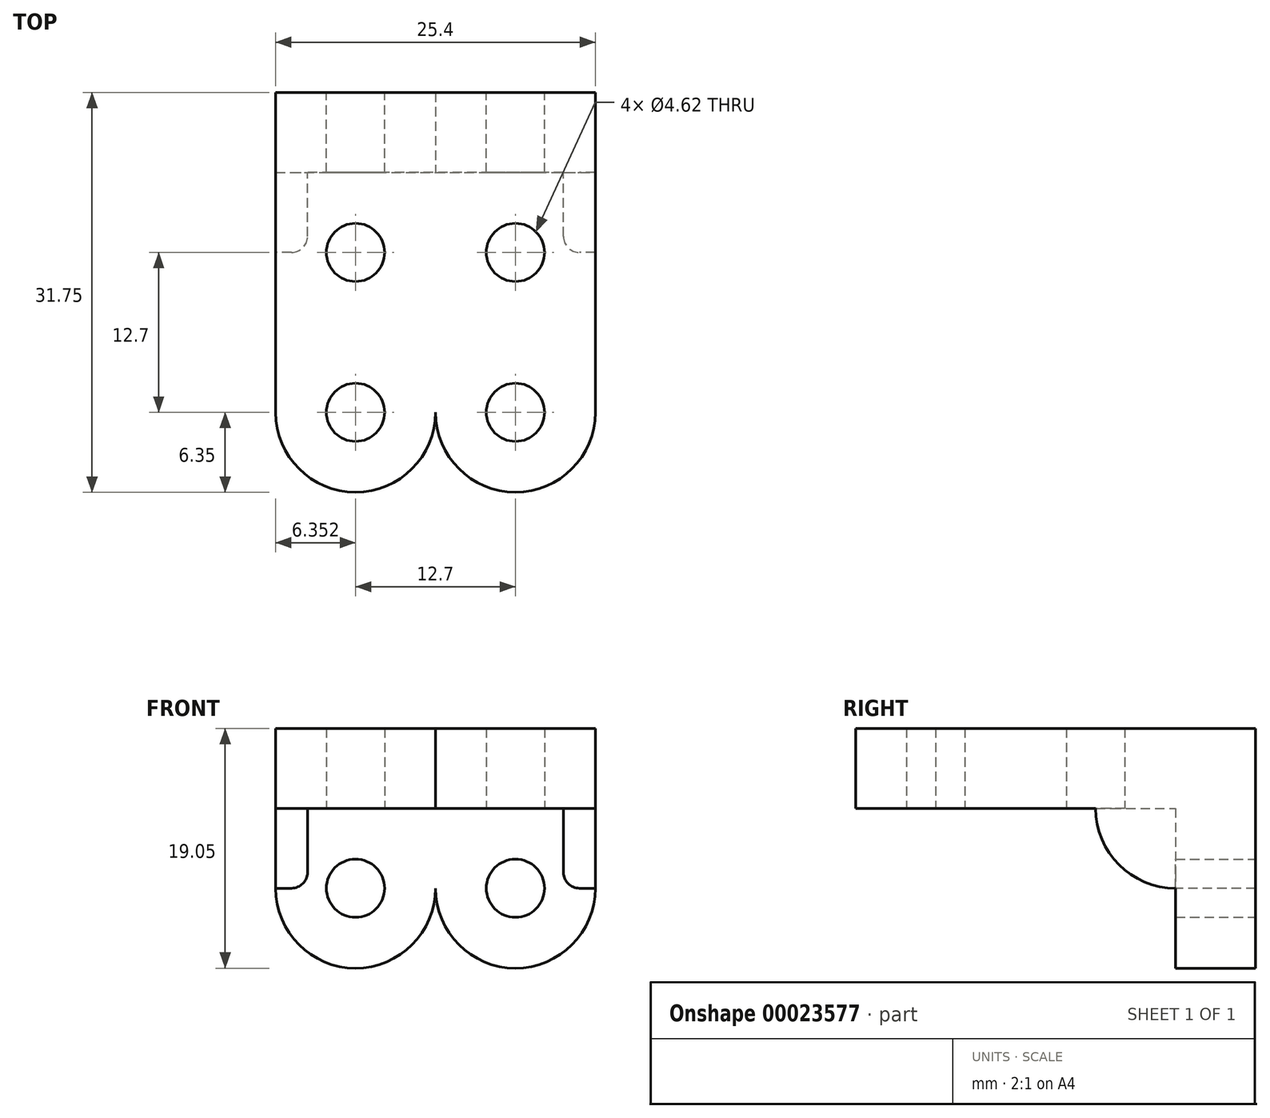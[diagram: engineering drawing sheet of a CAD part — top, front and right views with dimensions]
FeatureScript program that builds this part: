
annotation { "Feature Type Name" : "Feature", "Feature Type Description" : "" }
export const myFeature = defineFeature(function(context is Context, id is Id, definition is map)
    precondition{}
    {
        {
            var Q0;
            Q0=qCreatedBy(makeId("Front.planeOp"),FACE);
            var sketch = newSketch(context, id + "F0", { "sketchPlane" : qUnion([Q0])});
            skArc(sketch, "E0", {"start": v(-62.96, 0) * mm, "mid": v(-50.26, -12.7) * mm, "end": v(-37.56, 0) * mm});
            skLineSegment(sketch, "E1.top", {"start": v(-62.96, 12.7) * mm, "end": v(-37.56, 12.7) * mm});
            skLineSegment(sketch, "E1.left", {"start": v(-62.96, 0) * mm, "end": v(-62.96, 12.7) * mm});
            skLineSegment(sketch, "E1.right", {"start": v(-37.56, 0) * mm, "end": v(-37.56, 12.7) * mm});
            skLineSegment(sketch, "E2", {"start": v(-50.26, 0) * mm, "end": v(-43.9, 0) * mm});
            skLineSegment(sketch, "E3", {"start": v(-50.26, 0) * mm, "end": v(-56.6, 0) * mm});
            skCircle(sketch, "E4", {"center": v(-56.6, 0) * mm, "radius": 2.31 * mm});
            skCircle(sketch, "E5", {"center": v(-43.9, 0) * mm, "radius": 2.31 * mm});
            skSolve(sketch);
        }
        {
            var Q0;
            Q0=makeQuery(id+"F0.imprint","IMPRINT",FACE,{"disambiguationData":[TD([[makeQuery(id+"F0.imprint","IMPRINT",EDGE,{"derivedFrom":sQuery(id+"F0.wireOp",EDGE,"E0")}),1.0]])]});
            extrude(context, id + "F1", {"entities" : qUnion([Q0]), "depth" : 6.35 * mm});
        }
        {
            var Q0;
            Q0=makeQuery(id+"F1.opExtrude","CAP_FACE",FACE,{"disambiguationData":[OSD([sQuery(id+"F0.wireOp",EDGE,"E0"),sQuery(id+"F0.wireOp",EDGE,"E1.top"),sQuery(id+"F0.wireOp",EDGE,"E1.left"),sQuery(id+"F0.wireOp",EDGE,"E1.right"),sQuery(id+"F0.wireOp",EDGE,"E4"),sQuery(id+"F0.wireOp",EDGE,"E5")])],"isStart":false});
            var sketch = newSketch(context, id + "F2", { "sketchPlane" : qUnion([Q0])});
            skLineSegment(sketch, "E6.bottom", {"start": v(-37.56, 12.7) * mm, "end": v(-62.96, 12.7) * mm});
            skLineSegment(sketch, "E6.top", {"start": v(-37.56, 6.35) * mm, "end": v(-62.96, 6.35) * mm});
            skLineSegment(sketch, "E6.left", {"start": v(-37.56, 12.7) * mm, "end": v(-37.56, 6.35) * mm});
            skLineSegment(sketch, "E6.right", {"start": v(-62.96, 12.7) * mm, "end": v(-62.96, 6.35) * mm});
            skSolve(sketch);
        }
        {
            var Q0;
            Q0 = qSketchRegion(id + "F2", true);
            var Q1;
            Q1=makeQuery(id+"F2.imprint","IMPRINT",FACE,{"disambiguationData":[TD([[makeQuery(id+"F2.imprint","IMPRINT",EDGE,{"derivedFrom":sQuery(id+"F2.wireOp",EDGE,"E6.bottom")}),-1.0]])]});
            extrude(context, id + "F3", {"entities" : qUnion([Q0, Q1]), "operationType" : NewBodyOperationType.ADD, "depth" : 19.05 * mm});
        }
        {
            var Q0;
            Q0=makeQuery(id+"F3.opExtrude","CAP_FACE",FACE,{"disambiguationData":[OSD([sQuery(id+"F2.wireOp",EDGE,"E6.bottom"),sQuery(id+"F2.wireOp",EDGE,"E6.top"),sQuery(id+"F2.wireOp",EDGE,"E6.left"),sQuery(id+"F2.wireOp",EDGE,"E6.right")])],"isStart":false});
            extrude(context, id + "F4", {"entities" : qUnion([Q0]), "operationType" : NewBodyOperationType.ADD, "depth" : 12.7 * mm});
        }
        {
            var Q0;
            {var subQ0=sQuery(id+"F2.wireOp",EDGE,"E6.top");Q0=makeQuery(id+"F4.boolean.opBoolean","MERGE",FACE,{"derivedFrom":[makeQuery(id+"F3.opExtrude","SWEPT_FACE",FACE,{"disambiguationData":[OSD([subQ0])]}),makeQuery(id+"F4.opExtrude","SWEPT_FACE",FACE,{"disambiguationData":[OSD([subQ0])]})]});}
            var sketch = newSketch(context, id + "F5", { "sketchPlane" : qUnion([Q0])});
            skArc(sketch, "E7", {"start": v(-37.56, 25.4) * mm, "mid": v(-50.26, 38.1) * mm, "end": v(-62.96, 25.4) * mm});
            skCircle(sketch, "E8", {"center": v(-56.6, 25.4) * mm, "radius": 2.31 * mm});
            skCircle(sketch, "E9", {"center": v(-43.9, 25.4) * mm, "radius": 2.31 * mm});
            skCircle(sketch, "E10", {"center": v(-56.6, 12.7) * mm, "radius": 2.31 * mm});
            skCircle(sketch, "E11", {"center": v(-43.9, 12.7) * mm, "radius": 2.31 * mm});
            skSolve(sketch);
        }
        {
            var Q0;
            Q0 = qSketchRegion(id + "F5", true);
            var Q1;
            {var subQ1=sQuery(id+"F2.wireOp",EDGE,"E6.top");var subQ4=sQuery(id+"F5.wireOp",EDGE,"E7");var subQ6=makeQuery(id+"F4.opExtrude","CAP_EDGE",EDGE,{"disambiguationData":[OSD([subQ1])],"isStart":false});var subQ8=makeQuery(id+"F5.imprint","INTERSECT",VERTEX,{"derivedFrom":[subQ6,subQ4]});Q1=makeQuery(id+"F5.imprint","IMPRINT",FACE,{"disambiguationData":[TD([[makeQuery(id+"F5.imprint","IMPRINT",EDGE,{"disambiguationData":[TD([[subQ8,-1.0]])],"derivedFrom":subQ4}),-1.0]])]});}
            var Q2;
            {var subQ1=sQuery(id+"F2.wireOp",EDGE,"E6.top");var subQ4=sQuery(id+"F5.wireOp",EDGE,"E7");var subQ6=makeQuery(id+"F4.opExtrude","CAP_EDGE",EDGE,{"disambiguationData":[OSD([subQ1])],"isStart":false});var subQ8=makeQuery(id+"F5.imprint","INTERSECT",VERTEX,{"derivedFrom":[subQ6,subQ4]});Q2=makeQuery(id+"F5.imprint","IMPRINT",FACE,{"disambiguationData":[TD([[makeQuery(id+"F5.imprint","IMPRINT",EDGE,{"disambiguationData":[TD([[subQ8,1.0]])],"derivedFrom":subQ4}),-1.0]])]});}
            extrude(context, id + "F6", {"entities" : qUnion([Q0, Q1, Q2]), "operationType" : NewBodyOperationType.REMOVE, "oppositeDirection" : true, "depth" : 25.4 * mm});
        }
        {
            var Q0;
            Q0=makeQuery(id+"F1.opExtrude","CAP_FACE",FACE,{"disambiguationData":[OSD([sQuery(id+"F0.wireOp",EDGE,"E0"),sQuery(id+"F0.wireOp",EDGE,"E1.top"),sQuery(id+"F0.wireOp",EDGE,"E1.left"),sQuery(id+"F0.wireOp",EDGE,"E1.right"),sQuery(id+"F0.wireOp",EDGE,"E4"),sQuery(id+"F0.wireOp",EDGE,"E5")])],"isStart":false});
            var sketch = newSketch(context, id + "F7", { "sketchPlane" : qUnion([Q0])});
            skLineSegment(sketch, "E12.bottom", {"start": v(-37.56, 6.35) * mm, "end": v(-40.1, 6.35) * mm});
            skLineSegment(sketch, "E12.top", {"start": v(-37.56, 0) * mm, "end": v(-40.1, 0) * mm});
            skLineSegment(sketch, "E12.left", {"start": v(-37.56, 6.35) * mm, "end": v(-37.56, 0) * mm});
            skLineSegment(sketch, "E12.right", {"start": v(-40.1, 6.35) * mm, "end": v(-40.1, 0) * mm});
            skSolve(sketch);
        }
        {
            var Q0;
            Q0=makeQuery(id+"F7.imprint","IMPRINT",FACE,{"disambiguationData":[TD([[makeQuery(id+"F7.imprint","IMPRINT",EDGE,{"derivedFrom":sQuery(id+"F7.wireOp",EDGE,"E12.bottom")}),1.0]])]});
            extrude(context, id + "F8", {"entities" : qUnion([Q0]), "operationType" : NewBodyOperationType.ADD, "depth" : 6.35 * mm});
        }
        {
            var Q0;
            {var subQ0=sQuery(id+"F2.wireOp",EDGE,"E6.left");Q0=makeQuery(id+"F8.boolean.opBoolean","MERGE",FACE,{"derivedFrom":[makeQuery(id+"F4.boolean.opBoolean","MERGE",FACE,{"derivedFrom":[makeQuery(id+"F3.boolean.opBoolean","MERGE",FACE,{"derivedFrom":[makeQuery(id+"F1.opExtrude","SWEPT_FACE",FACE,{"disambiguationData":[OSD([sQuery(id+"F0.wireOp",EDGE,"E1.right")])]}),makeQuery(id+"F3.opExtrude","SWEPT_FACE",FACE,{"disambiguationData":[OSD([subQ0])]})]}),makeQuery(id+"F4.opExtrude","SWEPT_FACE",FACE,{"disambiguationData":[OSD([subQ0])]})]}),makeQuery(id+"F8.opExtrude","SWEPT_FACE",FACE,{"disambiguationData":[OSD([sQuery(id+"F7.wireOp",EDGE,"E12.left")])]})]});}
            var sketch = newSketch(context, id + "F9", { "sketchPlane" : qUnion([Q0])});
            skArc(sketch, "E13", {"start": v(-12.7, 6.35) * mm, "mid": v(-10.84, 1.86) * mm, "end": v(-6.35, 0) * mm});
            skSolve(sketch);
        }
        {
            var Q0;
            Q0 = qSketchRegion(id + "F9", true);
            var Q1;
            Q1=makeQuery(id+"F9.imprint","IMPRINT",FACE,{"disambiguationData":[TD([[makeQuery(id+"F9.imprint","IMPRINT",EDGE,{"derivedFrom":sQuery(id+"F9.wireOp",EDGE,"E13")}),-1.0]])]});
            extrude(context, id + "F10", {"entities" : qUnion([Q0, Q1]), "operationType" : NewBodyOperationType.REMOVE, "oppositeDirection" : true, "depth" : 25.4 * mm});
        }
        {
            var Q0;
            Q0=makeQuery(id+"F1.opExtrude","CAP_FACE",FACE,{"disambiguationData":[OSD([sQuery(id+"F0.wireOp",EDGE,"E0"),sQuery(id+"F0.wireOp",EDGE,"E1.top"),sQuery(id+"F0.wireOp",EDGE,"E1.left"),sQuery(id+"F0.wireOp",EDGE,"E1.right"),sQuery(id+"F0.wireOp",EDGE,"E4"),sQuery(id+"F0.wireOp",EDGE,"E5")])],"isStart":false});
            var sketch = newSketch(context, id + "F11", { "sketchPlane" : qUnion([Q0])});
            skLineSegment(sketch, "E14.bottom", {"start": v(-62.96, 6.35) * mm, "end": v(-60.42, 6.35) * mm});
            skLineSegment(sketch, "E14.top", {"start": v(-62.96, 0) * mm, "end": v(-60.42, 0) * mm});
            skLineSegment(sketch, "E14.left", {"start": v(-62.96, 6.35) * mm, "end": v(-62.96, 0) * mm});
            skLineSegment(sketch, "E14.right", {"start": v(-60.42, 6.35) * mm, "end": v(-60.42, 0) * mm});
            skSolve(sketch);
        }
        {
            var Q0;
            Q0 = qSketchRegion(id + "F11", true);
            extrude(context, id + "F12", {"entities" : qUnion([Q0]), "operationType" : NewBodyOperationType.ADD, "depth" : 6.35 * mm});
        }
        {
            var Q0;
            {var subQ0=sQuery(id+"F2.wireOp",EDGE,"E6.right");Q0=makeQuery(id+"F12.boolean.opBoolean","MERGE",FACE,{"derivedFrom":[makeQuery(id+"F4.boolean.opBoolean","MERGE",FACE,{"derivedFrom":[makeQuery(id+"F3.boolean.opBoolean","MERGE",FACE,{"derivedFrom":[makeQuery(id+"F1.opExtrude","SWEPT_FACE",FACE,{"disambiguationData":[OSD([sQuery(id+"F0.wireOp",EDGE,"E1.left")])]}),makeQuery(id+"F3.opExtrude","SWEPT_FACE",FACE,{"disambiguationData":[OSD([subQ0])]})]}),makeQuery(id+"F4.opExtrude","SWEPT_FACE",FACE,{"disambiguationData":[OSD([subQ0])]})]}),makeQuery(id+"F12.opExtrude","SWEPT_FACE",FACE,{"disambiguationData":[OSD([sQuery(id+"F11.wireOp",EDGE,"E14.left")])]})]});}
            var sketch = newSketch(context, id + "F13", { "sketchPlane" : qUnion([Q0])});
            skArc(sketch, "E15", {"start": v(6.35, 0) * mm, "mid": v(10.84, 1.86) * mm, "end": v(12.7, 6.35) * mm});
            skSolve(sketch);
        }
        {
            var Q0;
            Q0 = qSketchRegion(id + "F13", true);
            var Q1;
            Q1=makeQuery(id+"F13.imprint","IMPRINT",FACE,{"disambiguationData":[TD([[makeQuery(id+"F13.imprint","IMPRINT",EDGE,{"derivedFrom":sQuery(id+"F13.wireOp",EDGE,"E15")}),-1.0]])]});
            extrude(context, id + "F14", {"entities" : qUnion([Q0, Q1]), "operationType" : NewBodyOperationType.REMOVE, "oppositeDirection" : true, "depth" : 25.4 * mm});
        }
        {
            var Q0;
            {var subQ0=sQuery(id+"F2.wireOp",EDGE,"E6.top");Q0=makeQuery(id+"F4.boolean.opBoolean","MERGE",FACE,{"derivedFrom":[makeQuery(id+"F3.opExtrude","SWEPT_FACE",FACE,{"disambiguationData":[OSD([subQ0])]}),makeQuery(id+"F4.opExtrude","SWEPT_FACE",FACE,{"disambiguationData":[OSD([subQ0])]})]});}
            var sketch = newSketch(context, id + "F15", { "sketchPlane" : qUnion([Q0])});
            skLineSegment(sketch, "E16", {"start": v(-56.6, 25.4) * mm, "end": v(-56.6, 38.1) * mm});
            skCircle(sketch, "E17", {"center": v(-56.6, 38.1) * mm, "radius": 2.31 * mm});
            skSolve(sketch);
        }
        {
            var Q0;
            Q0 = qSketchRegion(id + "F15", true);
            extrude(context, id + "F16", {"entities" : qUnion([Q0]), "operationType" : NewBodyOperationType.REMOVE, "oppositeDirection" : true, "depth" : 25.4 * mm});
        }
        {
            var Q0;
            {var subQ0=sQuery(id+"F2.wireOp",EDGE,"E6.top");Q0=makeQuery(id+"F4.boolean.opBoolean","MERGE",FACE,{"derivedFrom":[makeQuery(id+"F3.opExtrude","SWEPT_FACE",FACE,{"disambiguationData":[OSD([subQ0])]}),makeQuery(id+"F4.opExtrude","SWEPT_FACE",FACE,{"disambiguationData":[OSD([subQ0])]})]});}
            var sketch = newSketch(context, id + "F17", { "sketchPlane" : qUnion([Q0])});
            skLineSegment(sketch, "E18", {"start": v(-43.9, 25.4) * mm, "end": v(-43.9, 38.1) * mm});
            skCircle(sketch, "E19", {"center": v(-43.9, 38.1) * mm, "radius": 2.31 * mm});
            skSolve(sketch);
        }
        {
            var Q0;
            Q0 = qSketchRegion(id + "F17", true);
            extrude(context, id + "F18", {"entities" : qUnion([Q0]), "operationType" : NewBodyOperationType.REMOVE, "oppositeDirection" : true, "depth" : 25.4 * mm});
        }
        {
            var Q0;
            {var subQ0=sQuery(id+"F2.wireOp",EDGE,"E6.top");Q0=makeQuery(id+"F4.boolean.opBoolean","MERGE",FACE,{"derivedFrom":[makeQuery(id+"F3.opExtrude","SWEPT_FACE",FACE,{"disambiguationData":[OSD([subQ0])]}),makeQuery(id+"F4.opExtrude","SWEPT_FACE",FACE,{"disambiguationData":[OSD([subQ0])]})]});}
            var sketch = newSketch(context, id + "F19", { "sketchPlane" : qUnion([Q0])});
            skArc(sketch, "E20", {"start": v(-50.26, 25.4) * mm, "mid": v(-56.6, 31.75) * mm, "end": v(-62.96, 25.4) * mm});
            skArc(sketch, "E21", {"start": v(-37.56, 25.4) * mm, "mid": v(-43.9, 31.75) * mm, "end": v(-50.26, 25.4) * mm});
            skSolve(sketch);
        }
        {
            var Q0;
            Q0 = qSketchRegion(id + "F19", true);
            var Q1;
            Q1=makeQuery(id+"F19.imprint","IMPRINT",FACE,{"disambiguationData":[TD([[makeQuery(id+"F19.imprint","IMPRINT",EDGE,{"derivedFrom":sQuery(id+"F19.wireOp",EDGE,"E20")}),-1.0]])]});
            extrude(context, id + "F20", {"entities" : qUnion([Q0, Q1]), "operationType" : NewBodyOperationType.REMOVE, "oppositeDirection" : true, "depth" : 25.4 * mm});
        }
        {
            var Q0;
            Q0=makeQuery(id+"F1.opExtrude","CAP_FACE",FACE,{"disambiguationData":[OSD([sQuery(id+"F0.wireOp",EDGE,"E0"),sQuery(id+"F0.wireOp",EDGE,"E1.top"),sQuery(id+"F0.wireOp",EDGE,"E1.left"),sQuery(id+"F0.wireOp",EDGE,"E1.right"),sQuery(id+"F0.wireOp",EDGE,"E4"),sQuery(id+"F0.wireOp",EDGE,"E5")])],"isStart":false});
            var sketch = newSketch(context, id + "F21", { "sketchPlane" : qUnion([Q0])});
            skArc(sketch, "E22", {"start": v(-62.96, 0) * mm, "mid": v(-56.6, -6.35) * mm, "end": v(-50.26, 0) * mm});
            skArc(sketch, "E23", {"start": v(-50.26, 0) * mm, "mid": v(-43.9, -6.35) * mm, "end": v(-37.56, 0) * mm});
            skArc(sketch, "E24", {"start": v(-62.96, 0) * mm, "mid": v(-50.26, -12.7) * mm, "end": v(-37.56, 0) * mm});
            skSolve(sketch);
        }
        {
            var Q0;
            Q0 = qSketchRegion(id + "F21", true);
            extrude(context, id + "F22", {"entities" : qUnion([Q0]), "operationType" : NewBodyOperationType.REMOVE, "oppositeDirection" : true, "depth" : 25.4 * mm});
        }
        {
            var Q0;
            Q0=makeQuery(id+"F14.boolean.opBoolean","COPY",EDGE,{"derivedFrom":makeQuery(id+"F14.opExtrude","CAP_EDGE",EDGE,{"disambiguationData":[OSD([sQuery(id+"F13.wireOp",EDGE,"E15")])],"isStart":true})});
            var Q1;
            Q1=makeQuery(id+"F10.boolean.opBoolean","INTERSECT",EDGE,{"derivedFrom":[makeQuery(id+"F8.opExtrude","SWEPT_FACE",FACE,{"disambiguationData":[OSD([sQuery(id+"F7.wireOp",EDGE,"E12.right")])]}),makeQuery(id+"F10.opExtrude","SWEPT_FACE",FACE,{"disambiguationData":[OSD([sQuery(id+"F9.wireOp",EDGE,"E13")])]})]});
            var Q2;
            Q2=makeQuery(id+"F10.boolean.opBoolean","COPY",EDGE,{"derivedFrom":makeQuery(id+"F10.opExtrude","CAP_EDGE",EDGE,{"disambiguationData":[OSD([sQuery(id+"F9.wireOp",EDGE,"E13")])],"isStart":true})});
            fillet(context, id + "F23", {"entities" : qUnion([Q0, Q1, Q2]), "radius" : 1.27 * mm, "tangentPropagation" : true, "allowEdgeOverflow" : false});
        }
        {
            var Q0;
            Q0=makeQuery(id+"F14.boolean.opBoolean","INTERSECT",EDGE,{"derivedFrom":[makeQuery(id+"F12.opExtrude","SWEPT_FACE",FACE,{"disambiguationData":[OSD([sQuery(id+"F11.wireOp",EDGE,"E14.right")])]}),makeQuery(id+"F14.opExtrude","SWEPT_FACE",FACE,{"disambiguationData":[OSD([sQuery(id+"F13.wireOp",EDGE,"E15")])]})]});
            fillet(context, id + "F24", {"entities" : qUnion([Q0]), "radius" : 1.27 * mm, "tangentPropagation" : true, "allowEdgeOverflow" : false});
        }
    });
